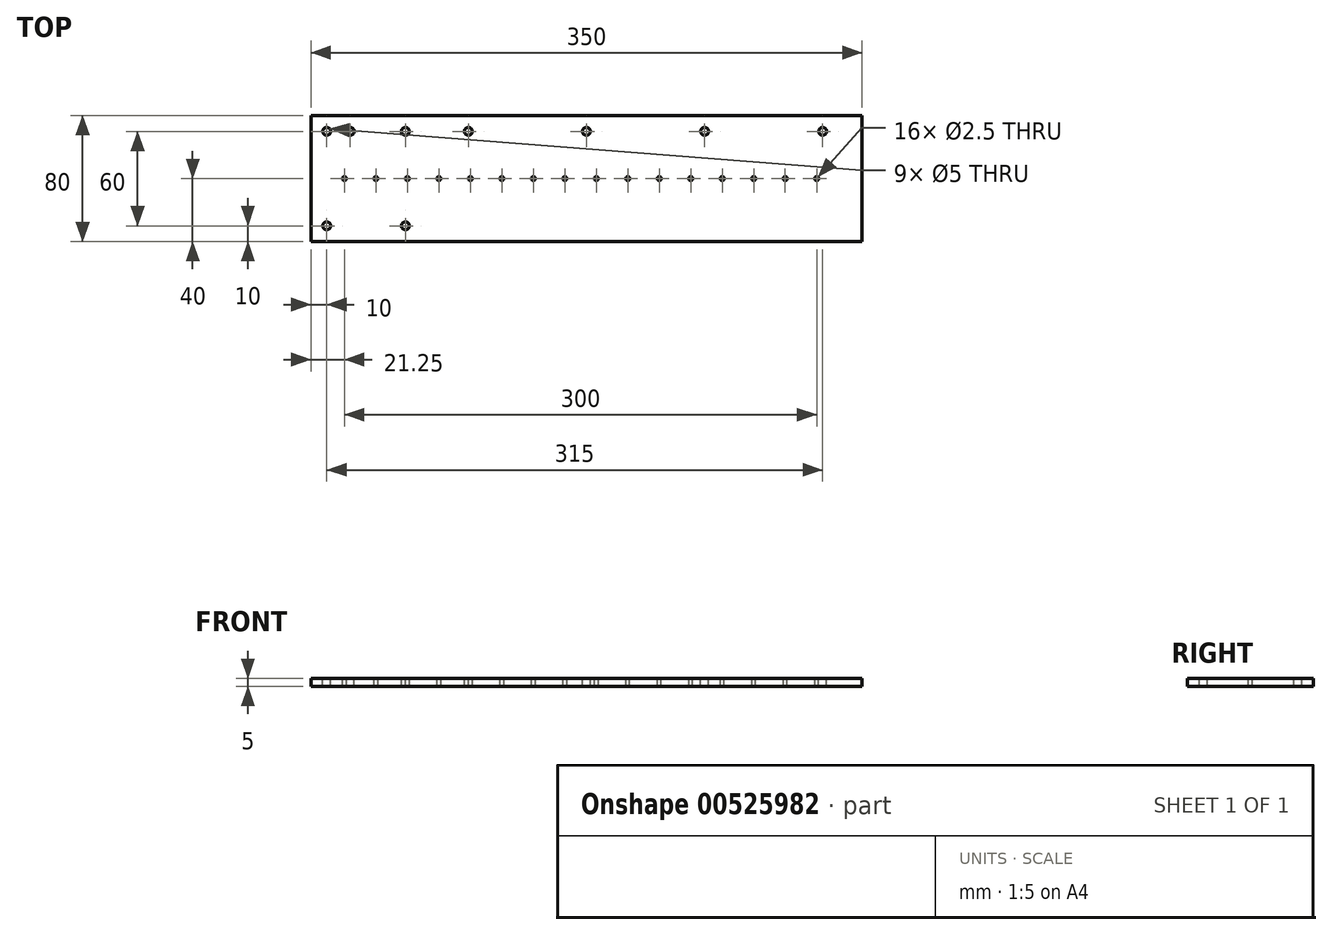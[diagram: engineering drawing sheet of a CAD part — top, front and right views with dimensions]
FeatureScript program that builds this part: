
annotation { "Feature Type Name" : "Feature", "Feature Type Description" : "" }
export const myFeature = defineFeature(function(context is Context, id is Id, definition is map)
    precondition{}
    {
        {
            var Q0;
            Q0=qCreatedBy(makeId("Top.planeOp"),FACE);
            var sketch = newSketch(context, id + "F0", { "sketchPlane" : qUnion([Q0])});
            skLineSegment(sketch, "E0.bottom", {"start": v(0, 0) * mm, "end": v(350, 0) * mm});
            skLineSegment(sketch, "E0.top", {"start": v(0, 80) * mm, "end": v(350, 80) * mm});
            skLineSegment(sketch, "E0.left", {"start": v(0, 0) * mm, "end": v(0, 80) * mm});
            skLineSegment(sketch, "E0.right", {"start": v(350, 0) * mm, "end": v(350, 80) * mm});
            skSolve(sketch);
        }
        {
            var Q0;
            Q0=makeQuery(id+"F0.imprint","IMPRINT",FACE,{"disambiguationData":[TD([[makeQuery(id+"F0.imprint","IMPRINT",EDGE,{"derivedFrom":sQuery(id+"F0.wireOp",EDGE,"E0.bottom")}),1.0]])]});
            extrude(context, id + "F1", {"entities" : qUnion([Q0]), "depth" : 5 * mm, "offsetDistance" : 25 * mm});
        }
        {
            var Q0;
            Q0=makeQuery(id+"F1.opExtrude","CAP_FACE",FACE,{"disambiguationData":[OSD([sQuery(id+"F0.wireOp",EDGE,"E0.bottom"),sQuery(id+"F0.wireOp",EDGE,"E0.top"),sQuery(id+"F0.wireOp",EDGE,"E0.left"),sQuery(id+"F0.wireOp",EDGE,"E0.right")])],"isStart":false});
            var sketch = newSketch(context, id + "F2", { "sketchPlane" : qUnion([Q0])});
            skLineSegment(sketch, "E1", {"start": v(0, 40) * mm, "end": v(350, 40) * mm, "construction": true});
            skCircle(sketch, "E2", {"center": v(21.25, 40) * mm, "radius": 1.25 * mm});
            skCircle(sketch, "E3.1.0.0", {"center": v(41.25, 40) * mm, "radius": 1.25 * mm});
            skCircle(sketch, "E3.2.0.0", {"center": v(61.25, 40) * mm, "radius": 1.25 * mm});
            skLineSegment(sketch, "E3.direction1", {"start": v(21.25, 40) * mm, "end": v(41.25, 40) * mm, "construction": true});
            skCircle(sketch, "E4.0.3.0", {"center": v(81.25, 40) * mm, "radius": 1.25 * mm});
            skCircle(sketch, "E4.0.4.0", {"center": v(101.25, 40) * mm, "radius": 1.25 * mm});
            skCircle(sketch, "E4.0.5.0", {"center": v(121.25, 40) * mm, "radius": 1.25 * mm});
            skCircle(sketch, "E4.0.6.0", {"center": v(141.25, 40) * mm, "radius": 1.25 * mm});
            skCircle(sketch, "E4.0.7.0", {"center": v(161.25, 40) * mm, "radius": 1.25 * mm});
            skCircle(sketch, "E4.0.8.0", {"center": v(181.25, 40) * mm, "radius": 1.25 * mm});
            skCircle(sketch, "E4.0.9.0", {"center": v(201.25, 40) * mm, "radius": 1.25 * mm});
            skCircle(sketch, "E4.0.10.0", {"center": v(221.25, 40) * mm, "radius": 1.25 * mm});
            skCircle(sketch, "E5.0.11.0", {"center": v(241.25, 40) * mm, "radius": 1.25 * mm});
            skCircle(sketch, "E5.0.12.0", {"center": v(261.25, 40) * mm, "radius": 1.25 * mm});
            skCircle(sketch, "E5.0.13.0", {"center": v(281.25, 40) * mm, "radius": 1.25 * mm});
            skCircle(sketch, "E5.0.14.0", {"center": v(301.25, 40) * mm, "radius": 1.25 * mm});
            skCircle(sketch, "E6.0.15.0", {"center": v(321.25, 40) * mm, "radius": 1.25 * mm});
            skSolve(sketch);
        }
        {
            var Q0;
            Q0 = qSketchRegion(id + "F2", true);
            extrude(context, id + "F3", {"entities" : qUnion([Q0]), "operationType" : NewBodyOperationType.REMOVE, "endBound" : BoundingType.THROUGH_ALL, "oppositeDirection" : true, "depth" : 25 * mm, "offsetDistance" : 25 * mm});
        }
        {
            var Q0;
            Q0=makeQuery(id+"F1.opExtrude","CAP_FACE",FACE,{"disambiguationData":[OSD([sQuery(id+"F0.wireOp",EDGE,"E0.bottom"),sQuery(id+"F0.wireOp",EDGE,"E0.top"),sQuery(id+"F0.wireOp",EDGE,"E0.left"),sQuery(id+"F0.wireOp",EDGE,"E0.right")])],"isStart":false});
            var sketch = newSketch(context, id + "F4", { "sketchPlane" : qUnion([Q0])});
            skLineSegment(sketch, "E7", {"start": v(350, 40) * mm, "end": v(0, 40) * mm, "construction": true});
            skPoint(sketch, "E8.direction2.start.orphan", {"position": v(340, 73.85) * mm});
            skSolve(sketch);
        }
        {
            var Q0;
            Q0=makeQuery(id+"F1.opExtrude","CAP_FACE",FACE,{"disambiguationData":[OSD([sQuery(id+"F0.wireOp",EDGE,"E0.bottom"),sQuery(id+"F0.wireOp",EDGE,"E0.top"),sQuery(id+"F0.wireOp",EDGE,"E0.left"),sQuery(id+"F0.wireOp",EDGE,"E0.right")])],"isStart":false});
            var sketch = newSketch(context, id + "F5", { "sketchPlane" : qUnion([Q0])});
            skLineSegment(sketch, "E9", {"start": v(0, 70) * mm, "end": v(350, 70) * mm, "construction": true});
            skCircle(sketch, "E10", {"center": v(25, 70) * mm, "radius": 2.5 * mm});
            skCircle(sketch, "E11.1.0.0", {"center": v(100, 70) * mm, "radius": 2.5 * mm});
            skCircle(sketch, "E11.2.0.0", {"center": v(175, 70) * mm, "radius": 2.5 * mm});
            skCircle(sketch, "E11.3.0.0", {"center": v(250, 70) * mm, "radius": 2.5 * mm});
            skCircle(sketch, "E11.4.0.0", {"center": v(325, 70) * mm, "radius": 2.5 * mm});
            skLineSegment(sketch, "E11.direction1", {"start": v(20, 70) * mm, "end": v(95, 70) * mm, "construction": true});
            skSolve(sketch);
        }
        {
            var Q0;
            Q0 = qSketchRegion(id + "F5", true);
            extrude(context, id + "F6", {"entities" : qUnion([Q0]), "operationType" : NewBodyOperationType.REMOVE, "oppositeDirection" : true, "depth" : 25 * mm, "offsetDistance" : 25 * mm});
        }
        {
            var Q0;
            Q0=makeQuery(id+"F4.imprint","IMPRINT",FACE,{"disambiguationData":[TD([[makeQuery(id+"F4.imprint","IMPRINT",EDGE,{"derivedFrom":makeQuery(id+"F1.opExtrude","CAP_EDGE",EDGE,{"disambiguationData":[OSD([sQuery(id+"F0.wireOp",EDGE,"E0.bottom")])],"isStart":false})}),1.0]])]});
            var sketch = newSketch(context, id + "F7", { "sketchPlane" : qUnion([Q0])});
            skCircle(sketch, "E12", {"center": v(10, 70) * mm, "radius": 2.5 * mm});
            skCircle(sketch, "E13.0.1.0", {"center": v(10, 10) * mm, "radius": 2.5 * mm});
            skCircle(sketch, "E13.1.0.0", {"center": v(60, 70) * mm, "radius": 2.5 * mm});
            skCircle(sketch, "E13.1.1.0", {"center": v(60, 10) * mm, "radius": 2.5 * mm});
            skLineSegment(sketch, "E13.direction1", {"start": v(10, 70) * mm, "end": v(60, 70) * mm, "construction": true});
            skLineSegment(sketch, "E13.direction2", {"start": v(10, 70) * mm, "end": v(10, 10) * mm, "construction": true});
            skSolve(sketch);
        }
        {
            var Q0;
            Q0 = qSketchRegion(id + "F7", true);
            extrude(context, id + "F8", {"entities" : qUnion([Q0]), "operationType" : NewBodyOperationType.REMOVE, "oppositeDirection" : true, "depth" : 25 * mm, "offsetDistance" : 25 * mm});
        }
    });
